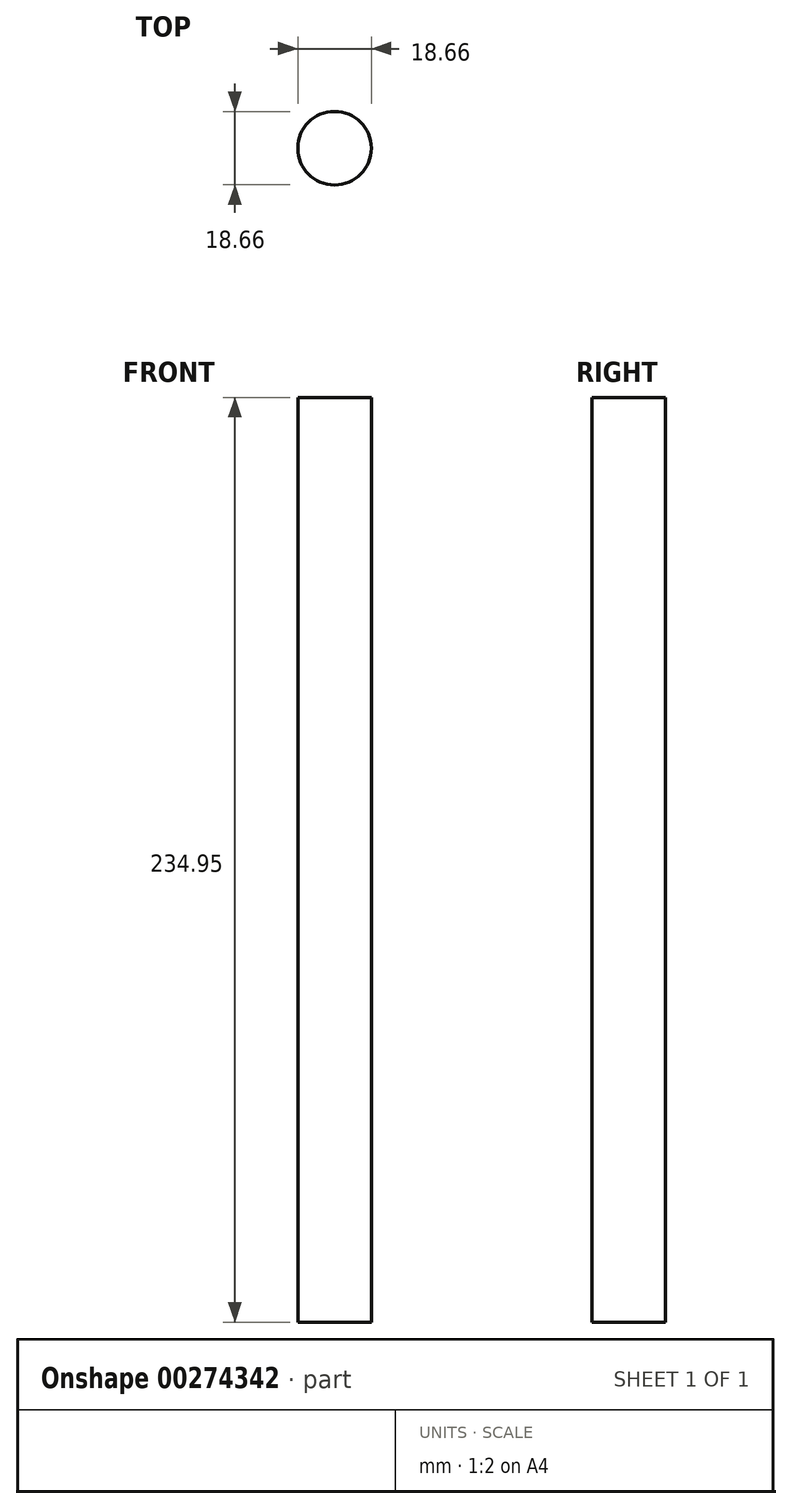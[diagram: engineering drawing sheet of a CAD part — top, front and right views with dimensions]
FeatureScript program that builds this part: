
annotation { "Feature Type Name" : "Feature", "Feature Type Description" : "" }
export const myFeature = defineFeature(function(context is Context, id is Id, definition is map)
    precondition{}
    {
        {
            var Q0;
            Q0=qCreatedBy(makeId("Top.planeOp"),FACE);
            var sketch = newSketch(context, id + "F0", { "sketchPlane" : qUnion([Q0])});
            skCircle(sketch, "E0", {"center": v(0, 0) * mm, "radius": 9.33 * mm});
            skSolve(sketch);
        }
        {
            var Q0;
            Q0 = qSketchRegion(id + "F0", true);
            extrude(context, id + "F1", {"entities" : qUnion([Q0]), "depth" : 234.95 * mm});
        }
    });
